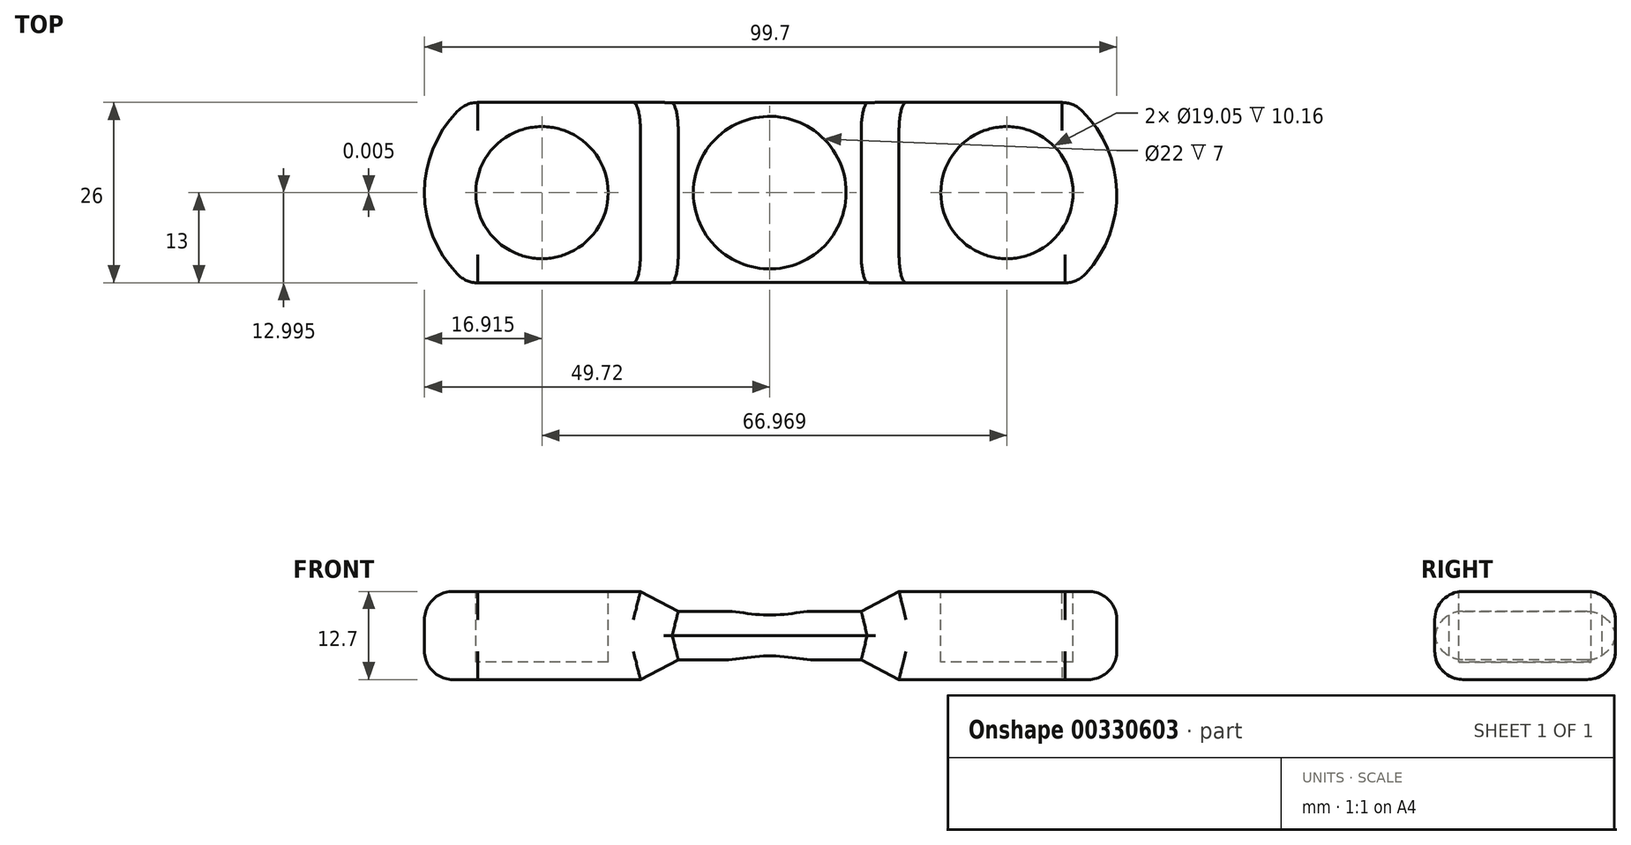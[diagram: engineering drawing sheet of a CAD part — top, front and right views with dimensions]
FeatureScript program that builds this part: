
annotation { "Feature Type Name" : "Feature", "Feature Type Description" : "" }
export const myFeature = defineFeature(function(context is Context, id is Id, definition is map)
    precondition{}
    {
        {
            var Q0;
            Q0=qCreatedBy(makeId("Top.planeOp"),FACE);
            var sketch = newSketch(context, id + "F0", { "sketchPlane" : qUnion([Q0])});
            skCircle(sketch, "E0", {"center": v(0, 0) * mm, "radius": 11 * mm});
            skLineSegment(sketch, "E1.bottom", {"start": v(-18.62, -13) * mm, "end": v(18.62, -13) * mm});
            skLineSegment(sketch, "E1.top", {"start": v(-18.62, 13) * mm, "end": v(18.62, 13) * mm});
            skLineSegment(sketch, "E1.left", {"start": v(-18.62, -13) * mm, "end": v(-18.62, 13) * mm});
            skLineSegment(sketch, "E1.right", {"start": v(18.62, -13) * mm, "end": v(18.62, 13) * mm});
            skArc(sketch, "E2", {"start": v(-43.62, 13) * mm, "mid": v(-49.72, 0) * mm, "end": v(-43.62, -13) * mm});
            skArc(sketch, "E3", {"start": v(44.14, -13) * mm, "mid": v(49.98, 0.12) * mm, "end": v(43.62, 13) * mm});
            skLineSegment(sketch, "E4", {"start": v(-43.62, 13) * mm, "end": v(-18.62, 13) * mm});
            skLineSegment(sketch, "E5", {"start": v(-43.62, -13) * mm, "end": v(-18.62, -13) * mm});
            skLineSegment(sketch, "E6", {"start": v(18.62, -13) * mm, "end": v(44.14, -13) * mm});
            skLineSegment(sketch, "E7", {"start": v(18.62, 13) * mm, "end": v(43.62, 13) * mm});
            skSolve(sketch);
        }
        {
            var Q0;
            Q0=makeQuery(id+"F0.imprint","IMPRINT",FACE,{"disambiguationData":[TD([[makeQuery(id+"F0.imprint","IMPRINT",EDGE,{"derivedFrom":sQuery(id+"F0.wireOp",EDGE,"E0")}),-1.0]])]});
            extrude(context, id + "F1", {"entities" : qUnion([Q0]), "endBound" : BoundingType.SYMMETRIC, "depth" : 7 * mm});
        }
        {
            var Q0;
            Q0=makeQuery(id+"F0.imprint","IMPRINT",FACE,{"disambiguationData":[TD([[makeQuery(id+"F0.imprint","IMPRINT",EDGE,{"derivedFrom":sQuery(id+"F0.wireOp",EDGE,"E1.left")}),1.0]])]});
            var Q1;
            Q1=makeQuery(id+"F0.imprint","IMPRINT",FACE,{"disambiguationData":[TD([[makeQuery(id+"F0.imprint","IMPRINT",EDGE,{"derivedFrom":sQuery(id+"F0.wireOp",EDGE,"E1.right")}),-1.0]])]});
            extrude(context, id + "F2", {"entities" : qUnion([Q0, Q1]), "operationType" : NewBodyOperationType.ADD, "endBound" : BoundingType.SYMMETRIC, "depth" : 12.7 * mm});
        }
        {
            var Q0;
            Q0=makeQuery(id+"F2.opExtrude","CAP_FACE",FACE,{"disambiguationData":[OSD([sQuery(id+"F0.wireOp",EDGE,"E1.left"),sQuery(id+"F0.wireOp",EDGE,"E2"),sQuery(id+"F0.wireOp",EDGE,"E4"),sQuery(id+"F0.wireOp",EDGE,"E5")])],"isStart":false});
            var sketch = newSketch(context, id + "F3", { "sketchPlane" : qUnion([Q0])});
            skPoint(sketch, "E8.centerSnap0", {"position": v(-27.43, 0) * mm});
            skCircle(sketch, "E9", {"center": v(-32.8, 0) * mm, "radius": 9.53 * mm});
            skCircle(sketch, "E10", {"center": v(34.16, 0) * mm, "radius": 9.53 * mm});
            skSolve(sketch);
        }
        {
            var Q0;
            Q0=makeQuery(id+"F2.boolean.opBoolean","MERGE",FACE,{"derivedFrom":[makeQuery(id+"F1.opExtrude","SWEPT_FACE",FACE,{"disambiguationData":[OSD([sQuery(id+"F0.wireOp",EDGE,"E1.bottom")])]}),makeQuery(id+"F2.opExtrude","SWEPT_FACE",FACE,{"disambiguationData":[OSD([sQuery(id+"F0.wireOp",EDGE,"E5")])]}),makeQuery(id+"F2.opExtrude","SWEPT_FACE",FACE,{"disambiguationData":[OSD([sQuery(id+"F0.wireOp",EDGE,"E6")])]})]});
            var sketch = newSketch(context, id + "F4", { "sketchPlane" : qUnion([Q0])});
            skLineSegment(sketch, "E11", {"start": v(-18.62, 6.35) * mm, "end": v(-13.18, 3.5) * mm});
            skLineSegment(sketch, "E12", {"start": v(18.62, 6.35) * mm, "end": v(13.18, 3.5) * mm});
            skLineSegment(sketch, "E13", {"start": v(18.62, -6.35) * mm, "end": v(13.18, -3.5) * mm});
            skLineSegment(sketch, "E14", {"start": v(-18.62, -6.35) * mm, "end": v(-13.18, -3.5) * mm});
            skSolve(sketch);
        }
        {
            var Q0;
            {var subQ0=sQuery(id+"F4.wireOp",EDGE,"E11");Q0=makeQuery(id+"F4.imprint","IMPRINT",FACE,{"disambiguationData":[TD([[makeQuery(id+"F4.imprint","IMPRINT",EDGE,{"derivedFrom":subQ0}),-1.0]])]});}
            var Q1;
            {var subQ0=sQuery(id+"F4.wireOp",EDGE,"E13");Q1=makeQuery(id+"F4.imprint","IMPRINT",FACE,{"disambiguationData":[TD([[makeQuery(id+"F4.imprint","IMPRINT",EDGE,{"derivedFrom":subQ0}),-1.0]])]});}
            var Q2;
            {var subQ0=sQuery(id+"F4.wireOp",EDGE,"E12");Q2=makeQuery(id+"F4.imprint","IMPRINT",FACE,{"disambiguationData":[TD([[makeQuery(id+"F4.imprint","IMPRINT",EDGE,{"derivedFrom":subQ0}),1.0]])]});}
            var Q3;
            {var subQ0=sQuery(id+"F4.wireOp",EDGE,"E14");Q3=makeQuery(id+"F4.imprint","IMPRINT",FACE,{"disambiguationData":[TD([[makeQuery(id+"F4.imprint","IMPRINT",EDGE,{"derivedFrom":subQ0}),1.0]])]});}
            extrude(context, id + "F5", {"entities" : qUnion([Q0, Q1, Q2, Q3]), "operationType" : NewBodyOperationType.ADD, "oppositeDirection" : true, "depth" : 26 * mm, "offsetDistance" : 25.4 * mm});
        }
        {
            var Q0;
            Q0=makeQuery(id+"F2.opExtrude","CAP_EDGE",EDGE,{"disambiguationData":[OSD([sQuery(id+"F0.wireOp",EDGE,"E5")])],"isStart":false});
            var Q1;
            Q1=makeQuery(id+"F1.opExtrude","CAP_EDGE",EDGE,{"disambiguationData":[OSD([sQuery(id+"F0.wireOp",EDGE,"E1.bottom")])],"isStart":false});
            var Q2;
            Q2=makeQuery(id+"F5.opExtrude","CAP_EDGE",EDGE,{"disambiguationData":[OSD([sQuery(id+"F4.wireOp",EDGE,"E11")])],"isStart":true});
            var Q3;
            Q3=makeQuery(id+"F5.opExtrude","CAP_EDGE",EDGE,{"disambiguationData":[OSD([sQuery(id+"F4.wireOp",EDGE,"E12")])],"isStart":true});
            var Q4;
            Q4=makeQuery(id+"F2.opExtrude","CAP_EDGE",EDGE,{"disambiguationData":[OSD([sQuery(id+"F0.wireOp",EDGE,"E6")])],"isStart":false});
            var Q5;
            Q5=makeQuery(id+"F2.opExtrude","CAP_EDGE",EDGE,{"disambiguationData":[OSD([sQuery(id+"F0.wireOp",EDGE,"E6")])],"isStart":true});
            var Q6;
            Q6=makeQuery(id+"F1.opExtrude","CAP_EDGE",EDGE,{"disambiguationData":[OSD([sQuery(id+"F0.wireOp",EDGE,"E1.bottom")])],"isStart":true});
            var Q7;
            Q7=makeQuery(id+"F5.opExtrude","CAP_EDGE",EDGE,{"disambiguationData":[OSD([sQuery(id+"F4.wireOp",EDGE,"E13")])],"isStart":true});
            var Q8;
            Q8=makeQuery(id+"F2.opExtrude","CAP_EDGE",EDGE,{"disambiguationData":[OSD([sQuery(id+"F0.wireOp",EDGE,"E5")])],"isStart":true});
            var Q9;
            Q9=makeQuery(id+"F5.opExtrude","CAP_EDGE",EDGE,{"disambiguationData":[OSD([sQuery(id+"F4.wireOp",EDGE,"E14")])],"isStart":true});
            var Q10;
            Q10=makeQuery(id+"F1.opExtrude","CAP_EDGE",EDGE,{"disambiguationData":[OSD([sQuery(id+"F0.wireOp",EDGE,"E1.top")])],"isStart":false});
            var Q11;
            Q11=makeQuery(id+"F2.opExtrude","CAP_EDGE",EDGE,{"disambiguationData":[OSD([sQuery(id+"F0.wireOp",EDGE,"E4")])],"isStart":false});
            var Q12;
            Q12=makeQuery(id+"F5.opExtrude","CAP_EDGE",EDGE,{"disambiguationData":[OSD([sQuery(id+"F4.wireOp",EDGE,"E11")])],"isStart":false});
            var Q13;
            Q13=makeQuery(id+"F2.opExtrude","CAP_EDGE",EDGE,{"disambiguationData":[OSD([sQuery(id+"F0.wireOp",EDGE,"E4")])],"isStart":true});
            var Q14;
            Q14=makeQuery(id+"F5.opExtrude","CAP_EDGE",EDGE,{"disambiguationData":[OSD([sQuery(id+"F4.wireOp",EDGE,"E14")])],"isStart":false});
            var Q15;
            Q15=makeQuery(id+"F1.opExtrude","CAP_EDGE",EDGE,{"disambiguationData":[OSD([sQuery(id+"F0.wireOp",EDGE,"E1.top")])],"isStart":true});
            var Q16;
            Q16=makeQuery(id+"F2.opExtrude","CAP_EDGE",EDGE,{"disambiguationData":[OSD([sQuery(id+"F0.wireOp",EDGE,"E7")])],"isStart":true});
            var Q17;
            Q17=makeQuery(id+"F5.opExtrude","CAP_EDGE",EDGE,{"disambiguationData":[OSD([sQuery(id+"F4.wireOp",EDGE,"E13")])],"isStart":false});
            var Q18;
            Q18=makeQuery(id+"F2.opExtrude","CAP_EDGE",EDGE,{"disambiguationData":[OSD([sQuery(id+"F0.wireOp",EDGE,"E7")])],"isStart":false});
            var Q19;
            Q19=makeQuery(id+"F5.opExtrude","CAP_EDGE",EDGE,{"disambiguationData":[OSD([sQuery(id+"F4.wireOp",EDGE,"E12")])],"isStart":false});
            fillet(context, id + "F6", {"entities" : qUnion([Q0, Q1, Q2, Q3, Q4, Q5, Q6, Q7, Q8, Q9, Q10, Q11, Q12, Q13, Q14, Q15, Q16, Q17, Q18, Q19]), "radius" : 4.06 * mm, "tangentPropagation" : true, "allowEdgeOverflow" : false});
        }
        {
            var Q0;
            Q0=makeQuery(id+"F2.opExtrude","CAP_EDGE",EDGE,{"disambiguationData":[OSD([sQuery(id+"F0.wireOp",EDGE,"E3")])],"isStart":true});
            var Q1;
            Q1=makeQuery(id+"F6.opFillet","BLEND_EDGE",EDGE,{"blendedFrom":[makeQuery(id+"F2.opExtrude","CAP_EDGE",EDGE,{"disambiguationData":[OSD([sQuery(id+"F0.wireOp",EDGE,"E7")])],"isStart":true}),makeQuery(id+"F2.opExtrude","SWEPT_FACE",FACE,{"disambiguationData":[OSD([sQuery(id+"F0.wireOp",EDGE,"E3")])]})],"blendedInto":[makeQuery(id+"F2.opExtrude","SWEPT_FACE",FACE,{"disambiguationData":[OSD([sQuery(id+"F0.wireOp",EDGE,"E3")])]})]});
            var Q2;
            Q2=makeQuery(id+"F6.opFillet","BLEND_EDGE",EDGE,{"blendedFrom":[makeQuery(id+"F2.opExtrude","CAP_EDGE",EDGE,{"disambiguationData":[OSD([sQuery(id+"F0.wireOp",EDGE,"E6")])],"isStart":false}),makeQuery(id+"F2.opExtrude","SWEPT_FACE",FACE,{"disambiguationData":[OSD([sQuery(id+"F0.wireOp",EDGE,"E3")])]})],"blendedInto":[makeQuery(id+"F2.opExtrude","SWEPT_FACE",FACE,{"disambiguationData":[OSD([sQuery(id+"F0.wireOp",EDGE,"E3")])]})]});
            var Q3;
            Q3=makeQuery(id+"F2.opExtrude","CAP_EDGE",EDGE,{"disambiguationData":[OSD([sQuery(id+"F0.wireOp",EDGE,"E3")])],"isStart":false});
            var Q4;
            Q4=makeQuery(id+"F2.opExtrude","SWEPT_EDGE",EDGE,{"disambiguationData":[OSD([sQuery(id+"F0.wireOp",EDGE,"E2"),sQuery(id+"F0.wireOp",EDGE,"E4")])]});
            var Q5;
            Q5=makeQuery(id+"F2.opExtrude","CAP_EDGE",EDGE,{"disambiguationData":[OSD([sQuery(id+"F0.wireOp",EDGE,"E2")])],"isStart":true});
            var Q6;
            Q6=makeQuery(id+"F6.opFillet","BLEND_EDGE",EDGE,{"blendedFrom":[makeQuery(id+"F2.opExtrude","CAP_EDGE",EDGE,{"disambiguationData":[OSD([sQuery(id+"F0.wireOp",EDGE,"E4")])],"isStart":false}),makeQuery(id+"F2.opExtrude","SWEPT_FACE",FACE,{"disambiguationData":[OSD([sQuery(id+"F0.wireOp",EDGE,"E2")])]})],"blendedInto":[makeQuery(id+"F2.opExtrude","SWEPT_FACE",FACE,{"disambiguationData":[OSD([sQuery(id+"F0.wireOp",EDGE,"E2")])]})]});
            var Q7;
            Q7=makeQuery(id+"F2.opExtrude","CAP_EDGE",EDGE,{"disambiguationData":[OSD([sQuery(id+"F0.wireOp",EDGE,"E2")])],"isStart":false});
            var Q8;
            Q8=makeQuery(id+"F6.opFillet","BLEND_EDGE",EDGE,{"blendedFrom":[makeQuery(id+"F2.opExtrude","CAP_EDGE",EDGE,{"disambiguationData":[OSD([sQuery(id+"F0.wireOp",EDGE,"E7")])],"isStart":false}),makeQuery(id+"F2.opExtrude","SWEPT_FACE",FACE,{"disambiguationData":[OSD([sQuery(id+"F0.wireOp",EDGE,"E3")])]})],"blendedInto":[makeQuery(id+"F2.opExtrude","SWEPT_FACE",FACE,{"disambiguationData":[OSD([sQuery(id+"F0.wireOp",EDGE,"E3")])]})]});
            var Q9;
            Q9=makeQuery(id+"F6.opFillet","BLEND_EDGE",EDGE,{"blendedFrom":[makeQuery(id+"F2.opExtrude","CAP_EDGE",EDGE,{"disambiguationData":[OSD([sQuery(id+"F0.wireOp",EDGE,"E6")])],"isStart":true}),makeQuery(id+"F2.opExtrude","SWEPT_FACE",FACE,{"disambiguationData":[OSD([sQuery(id+"F0.wireOp",EDGE,"E3")])]})],"blendedInto":[makeQuery(id+"F2.opExtrude","SWEPT_FACE",FACE,{"disambiguationData":[OSD([sQuery(id+"F0.wireOp",EDGE,"E3")])]})]});
            var Q10;
            Q10=makeQuery(id+"F2.opExtrude","SWEPT_EDGE",EDGE,{"disambiguationData":[OSD([sQuery(id+"F0.wireOp",EDGE,"E3"),sQuery(id+"F0.wireOp",EDGE,"E7")])]});
            var Q11;
            Q11=makeQuery(id+"F6.opFillet","BLEND_EDGE",EDGE,{"blendedFrom":[makeQuery(id+"F2.opExtrude","CAP_EDGE",EDGE,{"disambiguationData":[OSD([sQuery(id+"F0.wireOp",EDGE,"E4")])],"isStart":true}),makeQuery(id+"F2.opExtrude","SWEPT_FACE",FACE,{"disambiguationData":[OSD([sQuery(id+"F0.wireOp",EDGE,"E2")])]})],"blendedInto":[makeQuery(id+"F2.opExtrude","SWEPT_FACE",FACE,{"disambiguationData":[OSD([sQuery(id+"F0.wireOp",EDGE,"E2")])]})]});
            var Q12;
            Q12=makeQuery(id+"F6.opFillet","BLEND_EDGE",EDGE,{"blendedFrom":[makeQuery(id+"F2.opExtrude","CAP_EDGE",EDGE,{"disambiguationData":[OSD([sQuery(id+"F0.wireOp",EDGE,"E5")])],"isStart":false}),makeQuery(id+"F2.opExtrude","SWEPT_FACE",FACE,{"disambiguationData":[OSD([sQuery(id+"F0.wireOp",EDGE,"E2")])]})],"blendedInto":[makeQuery(id+"F2.opExtrude","SWEPT_FACE",FACE,{"disambiguationData":[OSD([sQuery(id+"F0.wireOp",EDGE,"E2")])]})]});
            var Q13;
            Q13=makeQuery(id+"F6.opFillet","BLEND_EDGE",EDGE,{"blendedFrom":[makeQuery(id+"F2.opExtrude","CAP_EDGE",EDGE,{"disambiguationData":[OSD([sQuery(id+"F0.wireOp",EDGE,"E5")])],"isStart":true}),makeQuery(id+"F2.opExtrude","SWEPT_FACE",FACE,{"disambiguationData":[OSD([sQuery(id+"F0.wireOp",EDGE,"E2")])]})],"blendedInto":[makeQuery(id+"F2.opExtrude","SWEPT_FACE",FACE,{"disambiguationData":[OSD([sQuery(id+"F0.wireOp",EDGE,"E2")])]})]});
            var Q14;
            Q14=makeQuery(id+"F2.opExtrude","SWEPT_EDGE",EDGE,{"disambiguationData":[OSD([sQuery(id+"F0.wireOp",EDGE,"E3"),sQuery(id+"F0.wireOp",EDGE,"E6")])]});
            var Q15;
            Q15=makeQuery(id+"F2.opExtrude","SWEPT_EDGE",EDGE,{"disambiguationData":[OSD([sQuery(id+"F0.wireOp",EDGE,"E2"),sQuery(id+"F0.wireOp",EDGE,"E5")])]});
            fillet(context, id + "F7", {"entities" : qUnion([Q0, Q1, Q2, Q3, Q4, Q5, Q6, Q7, Q8, Q9, Q10, Q11, Q12, Q13, Q14, Q15]), "radius" : 4.06 * mm, "tangentPropagation" : true, "allowEdgeOverflow" : false});
        }
        {
            var Q0;
            Q0 = qSketchRegion(id + "F3", true);
            extrude(context, id + "F8", {"entities" : qUnion([Q0]), "operationType" : NewBodyOperationType.REMOVE, "oppositeDirection" : true, "depth" : 10.16 * mm});
        }
    });
